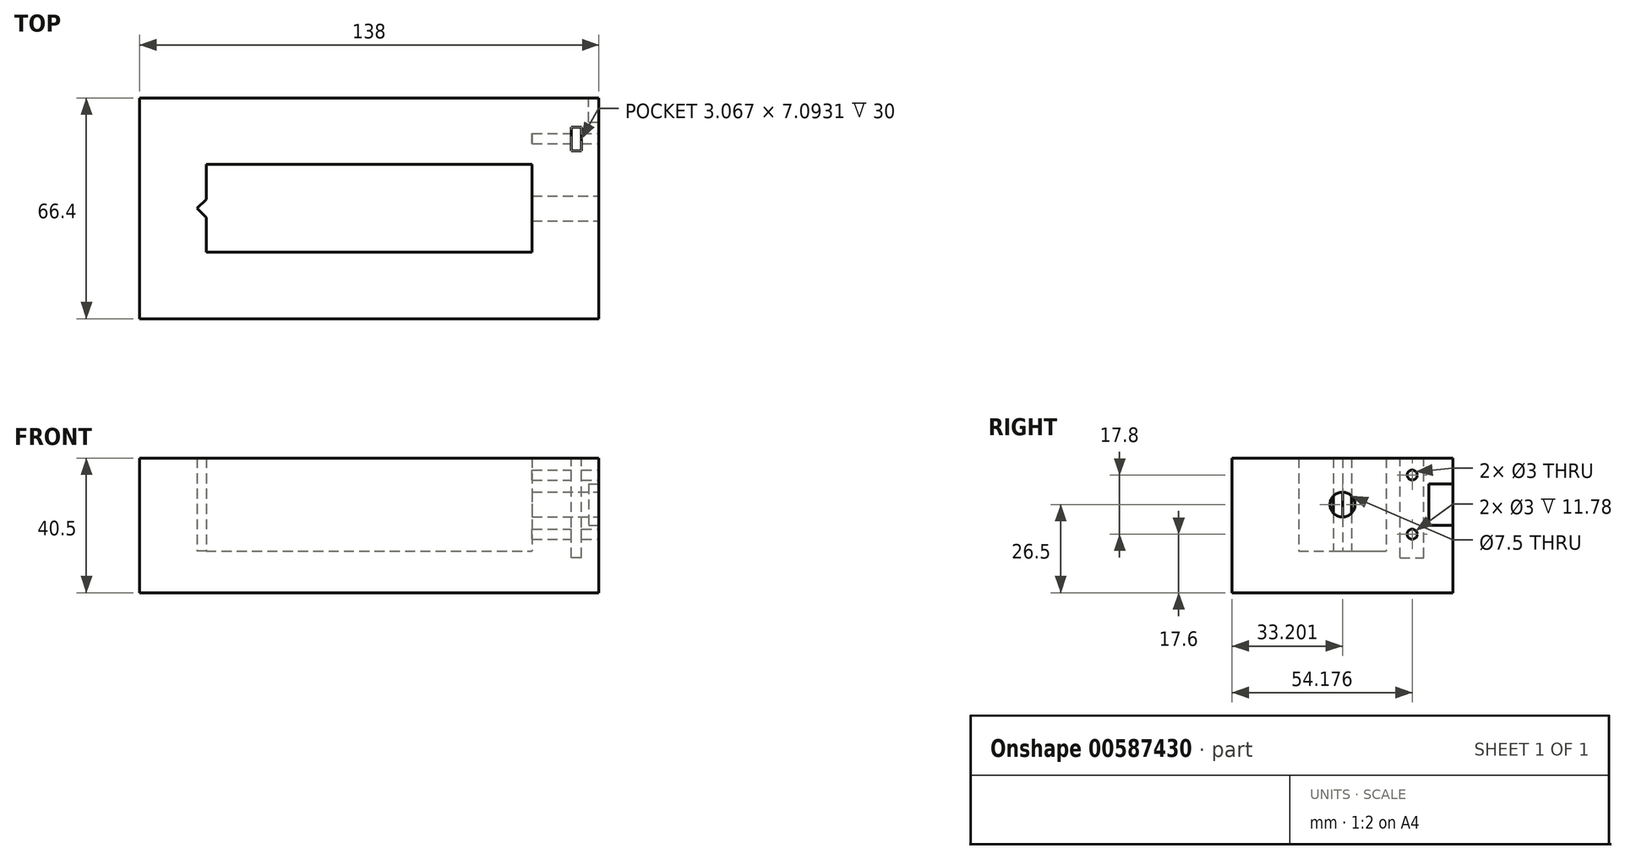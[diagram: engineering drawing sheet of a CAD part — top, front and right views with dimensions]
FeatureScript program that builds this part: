
annotation { "Feature Type Name" : "Feature", "Feature Type Description" : "" }
export const myFeature = defineFeature(function(context is Context, id is Id, definition is map)
    precondition{}
    {
        {
            var Q0;
            Q0=qCreatedBy(makeId("Top.planeOp"),FACE);
            var sketch = newSketch(context, id + "F0", { "sketchPlane" : qUnion([Q0])});
            skLineSegment(sketch, "E0.bottom", {"start": v(-76.1, 24.63) * mm, "end": v(61.9, 24.63) * mm});
            skLineSegment(sketch, "E0.top", {"start": v(-76.1, -41.77) * mm, "end": v(61.9, -41.77) * mm});
            skLineSegment(sketch, "E0.left", {"start": v(-76.1, 24.63) * mm, "end": v(-76.1, -41.77) * mm});
            skLineSegment(sketch, "E0.right", {"start": v(61.9, 24.63) * mm, "end": v(61.9, -41.77) * mm});
            skSolve(sketch);
        }
        {
            var Q0;
            Q0 = qSketchRegion(id + "F0", true);
            extrude(context, id + "F1", {"entities" : qUnion([Q0]), "depth" : 12.5 * mm, "offsetDistance" : 25 * mm});
        }
        {
            var Q0;
            Q0=makeQuery(id+"F1.opExtrude","CAP_FACE",FACE,{"disambiguationData":[OSD([sQuery(id+"F0.wireOp",EDGE,"E0.bottom"),sQuery(id+"F0.wireOp",EDGE,"E0.top"),sQuery(id+"F0.wireOp",EDGE,"E0.left"),sQuery(id+"F0.wireOp",EDGE,"E0.right")])],"isStart":false});
            var sketch = newSketch(context, id + "F2", { "sketchPlane" : qUnion([Q0])});
            skLineSegment(sketch, "E1.bottom", {"start": v(-76.1, -41.77) * mm, "end": v(61.9, -41.77) * mm});
            skLineSegment(sketch, "E1.top", {"start": v(-76.1, -21.77) * mm, "end": v(61.9, -21.77) * mm});
            skLineSegment(sketch, "E1.left", {"start": v(-76.1, -41.77) * mm, "end": v(-76.1, -21.77) * mm});
            skLineSegment(sketch, "E1.right", {"start": v(61.9, -41.77) * mm, "end": v(61.9, -21.77) * mm});
            skLineSegment(sketch, "E2.bottom", {"start": v(-76.1, 24.63) * mm, "end": v(61.9, 24.63) * mm});
            skLineSegment(sketch, "E2.top", {"start": v(-76.1, 4.63) * mm, "end": v(61.9, 4.63) * mm});
            skLineSegment(sketch, "E2.left", {"start": v(-76.1, 24.63) * mm, "end": v(-76.1, 4.63) * mm});
            skLineSegment(sketch, "E2.right", {"start": v(61.9, 24.63) * mm, "end": v(61.9, 4.63) * mm});
            skLineSegment(sketch, "E3", {"start": v(-76.1, -21.77) * mm, "end": v(-76.1, 4.63) * mm});
            skLineSegment(sketch, "E4", {"start": v(61.9, -21.77) * mm, "end": v(61.9, 4.63) * mm});
            skLineSegment(sketch, "E5", {"start": v(41.9, -21.77) * mm, "end": v(41.9, 4.63) * mm});
            skLineSegment(sketch, "E6", {"start": v(-56.1, -21.77) * mm, "end": v(-56.1, -11.32) * mm});
            skLineSegment(sketch, "E7", {"start": v(-56.1, -11.32) * mm, "end": v(-58.86, -8.57) * mm});
            skLineSegment(sketch, "E8", {"start": v(-58.86, -8.57) * mm, "end": v(-56.1, -5.82) * mm});
            skLineSegment(sketch, "E9", {"start": v(-56.1, -5.82) * mm, "end": v(-56.1, 4.63) * mm});
            skLineSegment(sketch, "E10", {"start": v(-58.86, -21.77) * mm, "end": v(-58.86, 4.63) * mm});
            skSolve(sketch);
        }
        {
            var Q0;
            Q0 = qSketchRegion(id + "F2", true);
            var Q1;
            {var subQ4=sQuery(id+"F2.wireOp",EDGE,"E8");Q1=makeQuery(id+"F2.imprint","IMPRINT",FACE,{"disambiguationData":[TD([[makeQuery(id+"F2.imprint","IMPRINT",EDGE,{"derivedFrom":subQ4}),1.0]])]});}
            var Q2;
            {var subQ0=sQuery(id+"F2.wireOp",EDGE,"E6");Q2=makeQuery(id+"F2.imprint","IMPRINT",FACE,{"disambiguationData":[TD([[makeQuery(id+"F2.imprint","IMPRINT",EDGE,{"derivedFrom":subQ0}),1.0]])]});}
            extrude(context, id + "F3", {"entities" : qUnion([Q0, Q1, Q2]), "operationType" : NewBodyOperationType.ADD, "depth" : 28 * mm, "offsetDistance" : 25 * mm});
        }
        {
            var Q0;
            Q0=makeQuery(id+"F3.boolean.opBoolean","MERGE",FACE,{"derivedFrom":[makeQuery(id+"F1.opExtrude","SWEPT_FACE",FACE,{"disambiguationData":[OSD([sQuery(id+"F0.wireOp",EDGE,"E0.right")])]}),makeQuery(id+"F3.opExtrude","SWEPT_FACE",FACE,{"disambiguationData":[OSD([sQuery(id+"F2.wireOp",EDGE,"E1.right"),sQuery(id+"F2.wireOp",EDGE,"E2.right"),sQuery(id+"F2.wireOp",EDGE,"E4")])]})]});
            var sketch = newSketch(context, id + "F4", { "sketchPlane" : qUnion([Q0])});
            skCircle(sketch, "E11", {"center": v(-8.57, 26.5) * mm, "radius": 3.75 * mm});
            skLineSegment(sketch, "E12", {"start": v(-8.57, 0) * mm, "end": v(-8.57, 40.5) * mm});
            skSolve(sketch);
        }
        {
            var Q0;
            Q0 = qSketchRegion(id + "F4", true);
            extrude(context, id + "F5", {"entities" : qUnion([Q0]), "operationType" : NewBodyOperationType.REMOVE, "oppositeDirection" : true, "depth" : 25 * mm, "offsetDistance" : 25 * mm});
        }
        {
            var Q0;
            Q0=makeQuery(id+"F3.boolean.opBoolean","MERGE",FACE,{"derivedFrom":[makeQuery(id+"F1.opExtrude","SWEPT_FACE",FACE,{"disambiguationData":[OSD([sQuery(id+"F0.wireOp",EDGE,"E0.right")])]}),makeQuery(id+"F3.opExtrude","SWEPT_FACE",FACE,{"disambiguationData":[OSD([sQuery(id+"F2.wireOp",EDGE,"E1.right"),sQuery(id+"F2.wireOp",EDGE,"E2.right"),sQuery(id+"F2.wireOp",EDGE,"E4")])]})]});
            var sketch = newSketch(context, id + "F6", { "sketchPlane" : qUnion([Q0])});
            skCircle(sketch, "E13", {"center": v(12.4, 35.4) * mm, "radius": 1.5 * mm});
            skCircle(sketch, "E14", {"center": v(12.4, 17.6) * mm, "radius": 1.5 * mm});
            skLineSegment(sketch, "E15", {"start": v(12.4, 17.6) * mm, "end": v(12.4, 35.4) * mm});
            skLineSegment(sketch, "E16", {"start": v(12.4, 26.5) * mm, "end": v(4.4, 26.5) * mm});
            skLineSegment(sketch, "E17", {"start": v(-4.82, 26.5) * mm, "end": v(0.4, 26.5) * mm});
            skLineSegment(sketch, "E18", {"start": v(0.4, 26.5) * mm, "end": v(4.4, 26.5) * mm});
            skCircle(sketch, "E19", {"center": v(2.4, 26.5) * mm, "radius": 2 * mm});
            skLineSegment(sketch, "E20", {"start": v(12.4, 26.5) * mm, "end": v(17.4, 26.5) * mm});
            skLineSegment(sketch, "E21", {"start": v(17.4, 26.5) * mm, "end": v(17.4, 20.32) * mm});
            skLineSegment(sketch, "E22", {"start": v(17.4, 26.5) * mm, "end": v(17.4, 32.68) * mm});
            skCircle(sketch, "E23", {"center": v(-8.57, 26.5) * mm, "radius": 3.75 * mm});
            skLineSegment(sketch, "E24", {"start": v(17.4, 32.68) * mm, "end": v(24.63, 32.68) * mm});
            skLineSegment(sketch, "E25", {"start": v(17.4, 20.32) * mm, "end": v(24.63, 20.32) * mm});
            skLineSegment(sketch, "E26", {"start": v(24.63, 20.32) * mm, "end": v(24.63, 32.68) * mm});
            skLineSegment(sketch, "E27", {"start": v(12.4, 35.4) * mm, "end": v(12.4, 40.5) * mm});
            skSolve(sketch);
        }
        {
            var Q0;
            Q0=makeQuery(id+"F6.imprint","IMPRINT",FACE,{"disambiguationData":[TD([[makeQuery(id+"F6.imprint","IMPRINT",EDGE,{"derivedFrom":sQuery(id+"F6.wireOp",EDGE,"E21")}),1.0]])]});
            extrude(context, id + "F7", {"entities" : qUnion([Q0]), "operationType" : NewBodyOperationType.REMOVE, "oppositeDirection" : true, "depth" : 3 * mm, "offsetDistance" : 25 * mm});
        }
        {
            var Q0;
            {var subQ0=sQuery(id+"F2.wireOp",EDGE,"E4");var subQ1=sQuery(id+"F2.wireOp",EDGE,"E2.right");var subQ2=sQuery(id+"F2.wireOp",EDGE,"E1.right");Q0=makeQuery(id+"FYjVbea7KTWOkHu_1.boolean.opBoolean","MERGE",FACE,{"derivedFrom":[makeQuery(id+"F3.opExtrude","CAP_FACE",FACE,{"disambiguationData":[OSD([sQuery(id+"F2.wireOp",EDGE,"E1.bottom"),sQuery(id+"F2.wireOp",EDGE,"E1.top"),sQuery(id+"F2.wireOp",EDGE,"E1.left"),subQ2,sQuery(id+"F2.wireOp",EDGE,"E2.bottom"),sQuery(id+"F2.wireOp",EDGE,"E2.top"),sQuery(id+"F2.wireOp",EDGE,"E2.left"),subQ1,sQuery(id+"F2.wireOp",EDGE,"E3"),subQ0,sQuery(id+"F2.wireOp",EDGE,"E5"),sQuery(id+"F2.wireOp",EDGE,"E6"),sQuery(id+"F2.wireOp",EDGE,"E7"),sQuery(id+"F2.wireOp",EDGE,"E8"),sQuery(id+"F2.wireOp",EDGE,"E9")])],"isStart":false}),makeQuery(id+"FYjVbea7KTWOkHu_1.opExtrude","SWEPT_FACE",FACE,{"disambiguationData":[OSD([subQ2,subQ1,subQ0])]})]});}
            var sketch = newSketch(context, id + "F8", { "sketchPlane" : qUnion([Q0])});
            skLineSegment(sketch, "E28", {"start": v(61.9, 12.28) * mm, "end": v(48.52, 12.28) * mm});
            skLineSegment(sketch, "E29.bottom", {"start": v(56.74, 8.73) * mm, "end": v(53.67, 8.73) * mm});
            skLineSegment(sketch, "E29.top", {"start": v(56.74, 15.83) * mm, "end": v(53.67, 15.83) * mm});
            skLineSegment(sketch, "E29.left", {"start": v(56.74, 8.73) * mm, "end": v(56.74, 15.83) * mm});
            skLineSegment(sketch, "E29.right", {"start": v(53.67, 8.73) * mm, "end": v(53.67, 15.83) * mm});
            skPoint(sketch, "E29.middle", {"position": v(55.2, 12.28) * mm});
            skSolve(sketch);
        }
        {
            var Q0;
            Q0=makeQuery(id+"F6.imprint","IMPRINT",FACE,{"disambiguationData":[TD([[makeQuery(id+"F6.imprint","IMPRINT",EDGE,{"derivedFrom":sQuery(id+"F6.wireOp",EDGE,"E14")}),1.0]])]});
            var Q1;
            {var subQ0=sQuery(id+"F6.wireOp",EDGE,"E15");var subQ1=sQuery(id+"F6.wireOp",EDGE,"E13");var subQ2=makeQuery(id+"F6.imprint","INTERSECT",VERTEX,{"derivedFrom":[subQ1,subQ0]});Q1=makeQuery(id+"F6.imprint","IMPRINT",FACE,{"disambiguationData":[TD([[makeQuery(id+"F6.imprint","IMPRINT",EDGE,{"disambiguationData":[TD([[subQ2,-1.0]])],"derivedFrom":subQ1}),1.0]])]});}
            var Q2;
            {var subQ0=sQuery(id+"F6.wireOp",EDGE,"E15");var subQ1=sQuery(id+"F6.wireOp",EDGE,"E13");var subQ2=makeQuery(id+"F6.imprint","INTERSECT",VERTEX,{"derivedFrom":[subQ1,subQ0]});Q2=makeQuery(id+"F6.imprint","IMPRINT",FACE,{"disambiguationData":[TD([[makeQuery(id+"F6.imprint","IMPRINT",EDGE,{"disambiguationData":[TD([[subQ2,1.0]])],"derivedFrom":subQ1}),1.0]])]});}
            extrude(context, id + "F9", {"entities" : qUnion([Q0, Q1, Q2]), "operationType" : NewBodyOperationType.REMOVE, "oppositeDirection" : true, "depth" : 20 * mm, "offsetDistance" : 25 * mm});
        }
        {
            var Q0;
            {var subQ0=sQuery(id+"F6.wireOp",EDGE,"E15");var subQ1=sQuery(id+"F6.wireOp",EDGE,"E13");var subQ2=makeQuery(id+"F6.imprint","INTERSECT",VERTEX,{"derivedFrom":[subQ1,subQ0]});Q0=makeQuery(id+"F6.imprint","IMPRINT",FACE,{"disambiguationData":[TD([[makeQuery(id+"F6.imprint","IMPRINT",EDGE,{"disambiguationData":[TD([[subQ2,1.0]])],"derivedFrom":subQ1}),1.0]])]});}
            var Q1;
            {var subQ0=sQuery(id+"F6.wireOp",EDGE,"E15");var subQ1=sQuery(id+"F6.wireOp",EDGE,"E13");var subQ2=makeQuery(id+"F6.imprint","INTERSECT",VERTEX,{"derivedFrom":[subQ1,subQ0]});Q1=makeQuery(id+"F6.imprint","IMPRINT",FACE,{"disambiguationData":[TD([[makeQuery(id+"F6.imprint","IMPRINT",EDGE,{"disambiguationData":[TD([[subQ2,-1.0]])],"derivedFrom":subQ1}),1.0]])]});}
            var Q2;
            Q2=makeQuery(id+"F6.imprint","IMPRINT",FACE,{"disambiguationData":[TD([[makeQuery(id+"F6.imprint","IMPRINT",EDGE,{"derivedFrom":sQuery(id+"F6.wireOp",EDGE,"E14")}),1.0]])]});
            extrude(context, id + "F10", {"entities" : qUnion([Q0, Q1, Q2]), "operationType" : NewBodyOperationType.REMOVE, "oppositeDirection" : true, "depth" : 15 * mm, "offsetDistance" : 25 * mm});
        }
        {
            var Q0;
            Q0 = qSketchRegion(id + "F8", true);
            extrude(context, id + "F11", {"entities" : qUnion([Q0]), "operationType" : NewBodyOperationType.REMOVE, "oppositeDirection" : true, "depth" : 30 * mm, "offsetDistance" : 25 * mm});
        }
    });
